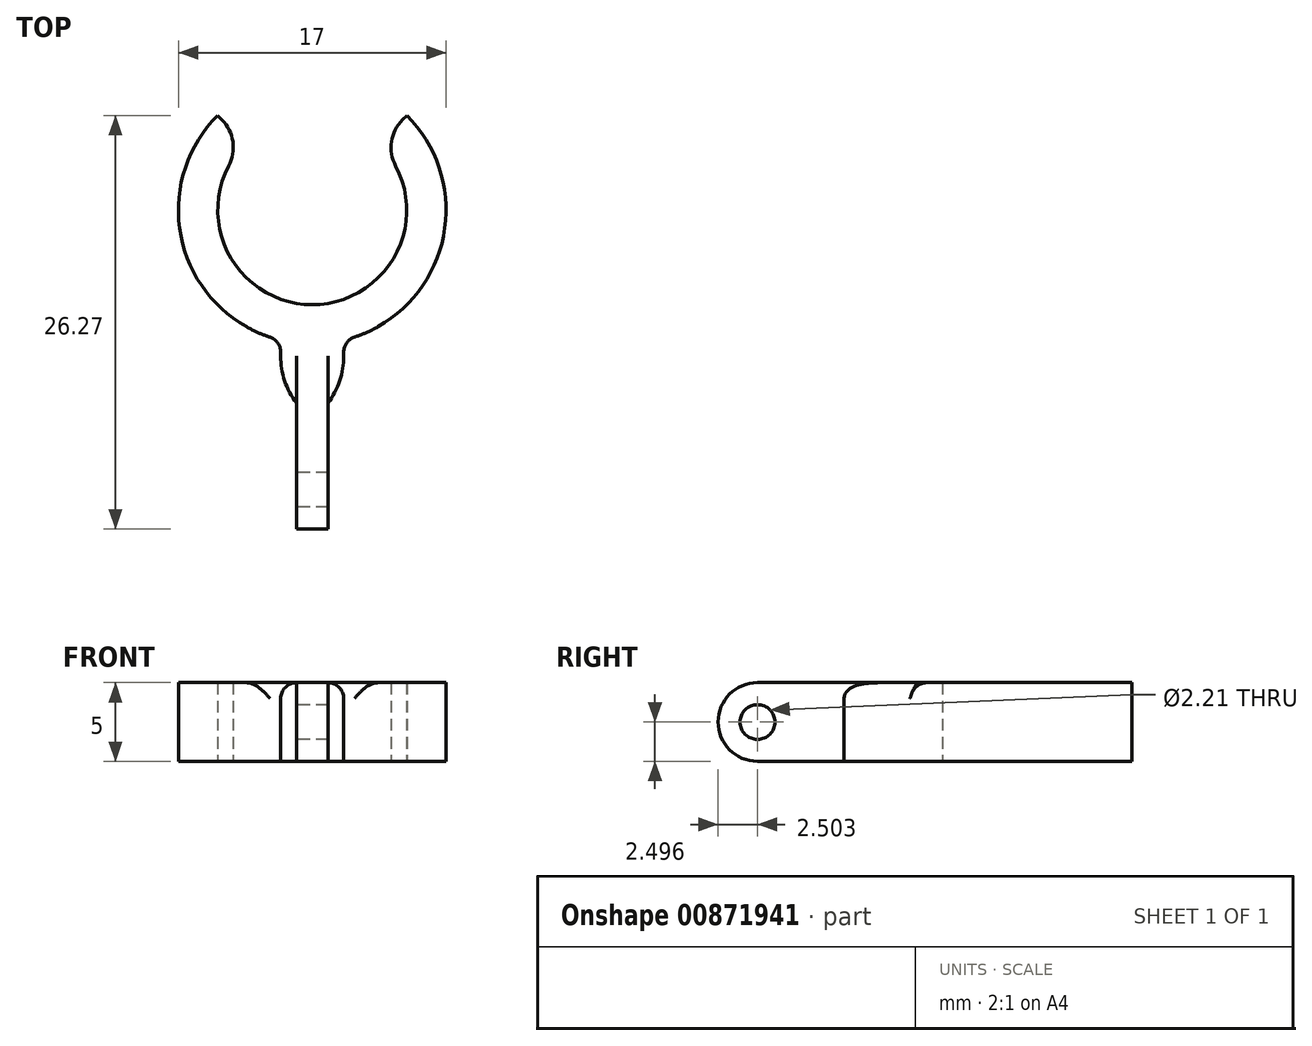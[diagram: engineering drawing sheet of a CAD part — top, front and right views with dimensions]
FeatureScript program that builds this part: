
annotation { "Feature Type Name" : "Feature", "Feature Type Description" : "" }
export const myFeature = defineFeature(function(context is Context, id is Id, definition is map)
    precondition{}
    {
        {
            var Q0;
            Q0=qCreatedBy(makeId("Top.planeOp"),FACE);
            var sketch = newSketch(context, id + "F0", { "sketchPlane" : qUnion([Q0])});
            skArc(sketch, "E0", {"start": v(-4.24, 4.24) * mm, "mid": v(0, -6) * mm, "end": v(4.24, 4.24) * mm});
            skArc(sketch, "E1", {"start": v(-6.01, 6.01) * mm, "mid": v(-8.18, -2.3) * mm, "end": v(-2, -8.26) * mm});
            skLineSegment(sketch, "E2", {"start": v(0, 15.66) * mm, "end": v(0, -18.54) * mm, "construction": true});
            skLineSegment(sketch, "E3", {"start": v(-4.24, 4.24) * mm, "end": v(-6.01, 6.01) * mm});
            skLineSegment(sketch, "E4", {"start": v(4.24, 4.24) * mm, "end": v(6.01, 6.01) * mm});
            skLineSegment(sketch, "E5", {"start": v(-2, -8.26) * mm, "end": v(-2, -12.26) * mm});
            skLineSegment(sketch, "E6", {"start": v(-2, -12.26) * mm, "end": v(-1, -12.26) * mm});
            skLineSegment(sketch, "E7", {"start": v(-1, -12.26) * mm, "end": v(-1, -20.26) * mm});
            skLineSegment(sketch, "E8", {"start": v(-1, -20.26) * mm, "end": v(0, -20.26) * mm});
            skLineSegment(sketch, "E9.MirrorCS", {"start": v(2, -8.26) * mm, "end": v(2, -12.26) * mm});
            skLineSegment(sketch, "E10.MirrorCS", {"start": v(2, -12.26) * mm, "end": v(1, -12.26) * mm});
            skLineSegment(sketch, "E11.MirrorCS", {"start": v(1, -12.26) * mm, "end": v(1, -20.26) * mm});
            skLineSegment(sketch, "E12.MirrorCS", {"start": v(1, -20.26) * mm, "end": v(0, -20.26) * mm});
            skArc(sketch, "E13.trimOffspring", {"start": v(2, -8.26) * mm, "mid": v(8.18, -2.3) * mm, "end": v(6.01, 6.01) * mm});
            skSolve(sketch);
        }
        {
            var Q0;
            Q0 = qSketchRegion(id + "F0", true);
            extrude(context, id + "F1", {"entities" : qUnion([Q0]), "depth" : 5 * mm, "offsetDistance" : 25 * mm});
        }
        {
            var Q0;
            Q0=makeQuery(id+"F1.opExtrude","SWEPT_FACE",FACE,{"disambiguationData":[OSD([sQuery(id+"F0.wireOp",EDGE,"E7")])]});
            var sketch = newSketch(context, id + "F2", { "sketchPlane" : qUnion([Q0])});
            skCircle(sketch, "E14", {"center": v(17.76, 2.5) * mm, "radius": 1.1 * mm});
            skSolve(sketch);
        }
        {
            var Q0;
            Q0=makeQuery(id+"F2.imprint","IMPRINT",FACE,{"disambiguationData":[TD([[makeQuery(id+"F2.imprint","IMPRINT",EDGE,{"derivedFrom":sQuery(id+"F2.wireOp",EDGE,"E14")}),1.0]])]});
            extrude(context, id + "F3", {"entities" : qUnion([Q0]), "operationType" : NewBodyOperationType.REMOVE, "oppositeDirection" : true, "depth" : 5 * mm, "offsetDistance" : 25 * mm});
        }
        {
            var Q0;
            Q0=makeQuery(id+"F1.opExtrude","SWEPT_EDGE",EDGE,{"disambiguationData":[OSD([sQuery(id+"F0.wireOp",EDGE,"E0"),sQuery(id+"F0.wireOp",EDGE,"E4")])]});
            var Q1;
            Q1=makeQuery(id+"F1.opExtrude","SWEPT_EDGE",EDGE,{"disambiguationData":[OSD([sQuery(id+"F0.wireOp",EDGE,"E0"),sQuery(id+"F0.wireOp",EDGE,"E3")])]});
            fillet(context, id + "F4", {"entities" : qUnion([Q0, Q1]), "radius" : 2.5 * mm, "tangentPropagation" : true, "allowEdgeOverflow" : false});
        }
        {
            var Q0;
            Q0=makeQuery(id+"F1.opExtrude","SWEPT_EDGE",EDGE,{"disambiguationData":[OSD([sQuery(id+"F0.wireOp",EDGE,"E9.MirrorCS"),sQuery(id+"F0.wireOp",EDGE,"E10.MirrorCS")])]});
            var Q1;
            Q1=makeQuery(id+"F1.opExtrude","SWEPT_EDGE",EDGE,{"disambiguationData":[OSD([sQuery(id+"F0.wireOp",EDGE,"E5"),sQuery(id+"F0.wireOp",EDGE,"E6")])]});
            fillet(context, id + "F5", {"entities" : qUnion([Q0, Q1]), "radius" : 5 * mm, "tangentPropagation" : true, "allowEdgeOverflow" : false});
        }
        {
            var Q0;
            Q0=makeQuery(id+"F1.opExtrude","SWEPT_EDGE",EDGE,{"disambiguationData":[OSD([sQuery(id+"F0.wireOp",EDGE,"E1"),sQuery(id+"F0.wireOp",EDGE,"E5")])]});
            var Q1;
            Q1=makeQuery(id+"F1.opExtrude","SWEPT_EDGE",EDGE,{"disambiguationData":[OSD([sQuery(id+"F0.wireOp",EDGE,"E9.MirrorCS"),sQuery(id+"F0.wireOp",EDGE,"E13.trimOffspring")])]});
            var Q2;
            {var subQ0=sQuery(id+"F0.wireOp",EDGE,"E10.MirrorCS");var subQ1=sQuery(id+"F0.wireOp",EDGE,"E9.MirrorCS");Q2=makeQuery(id+"F5.opFillet","BLEND_EDGE",EDGE,{"blendedFrom":[makeQuery(id+"F1.opExtrude","SWEPT_EDGE",EDGE,{"disambiguationData":[OSD([subQ1,subQ0])]}),makeQuery(id+"F1.opExtrude","CAP_FACE",FACE,{"disambiguationData":[OSD([sQuery(id+"F0.wireOp",EDGE,"E0"),sQuery(id+"F0.wireOp",EDGE,"E1"),sQuery(id+"F0.wireOp",EDGE,"E3"),sQuery(id+"F0.wireOp",EDGE,"E4"),sQuery(id+"F0.wireOp",EDGE,"E5"),sQuery(id+"F0.wireOp",EDGE,"E6"),sQuery(id+"F0.wireOp",EDGE,"E7"),sQuery(id+"F0.wireOp",EDGE,"E8"),subQ1,subQ0,sQuery(id+"F0.wireOp",EDGE,"E11.MirrorCS"),sQuery(id+"F0.wireOp",EDGE,"E12.MirrorCS"),sQuery(id+"F0.wireOp",EDGE,"E13.trimOffspring")])],"isStart":false})],"blendedInto":[makeQuery(id+"F1.opExtrude","CAP_FACE",FACE,{"disambiguationData":[OSD([sQuery(id+"F0.wireOp",EDGE,"E0"),sQuery(id+"F0.wireOp",EDGE,"E1"),sQuery(id+"F0.wireOp",EDGE,"E3"),sQuery(id+"F0.wireOp",EDGE,"E4"),sQuery(id+"F0.wireOp",EDGE,"E5"),sQuery(id+"F0.wireOp",EDGE,"E6"),sQuery(id+"F0.wireOp",EDGE,"E7"),sQuery(id+"F0.wireOp",EDGE,"E8"),subQ1,subQ0,sQuery(id+"F0.wireOp",EDGE,"E11.MirrorCS"),sQuery(id+"F0.wireOp",EDGE,"E12.MirrorCS"),sQuery(id+"F0.wireOp",EDGE,"E13.trimOffspring")])],"isStart":false})]});}
            var Q3;
            {var subQ0=sQuery(id+"F0.wireOp",EDGE,"E6");var subQ1=sQuery(id+"F0.wireOp",EDGE,"E5");Q3=makeQuery(id+"F5.opFillet","BLEND_EDGE",EDGE,{"blendedFrom":[makeQuery(id+"F1.opExtrude","SWEPT_EDGE",EDGE,{"disambiguationData":[OSD([subQ1,subQ0])]}),makeQuery(id+"F1.opExtrude","CAP_FACE",FACE,{"disambiguationData":[OSD([sQuery(id+"F0.wireOp",EDGE,"E0"),sQuery(id+"F0.wireOp",EDGE,"E1"),sQuery(id+"F0.wireOp",EDGE,"E3"),sQuery(id+"F0.wireOp",EDGE,"E4"),subQ1,subQ0,sQuery(id+"F0.wireOp",EDGE,"E7"),sQuery(id+"F0.wireOp",EDGE,"E8"),sQuery(id+"F0.wireOp",EDGE,"E9.MirrorCS"),sQuery(id+"F0.wireOp",EDGE,"E10.MirrorCS"),sQuery(id+"F0.wireOp",EDGE,"E11.MirrorCS"),sQuery(id+"F0.wireOp",EDGE,"E12.MirrorCS"),sQuery(id+"F0.wireOp",EDGE,"E13.trimOffspring")])],"isStart":false})],"blendedInto":[makeQuery(id+"F1.opExtrude","CAP_FACE",FACE,{"disambiguationData":[OSD([sQuery(id+"F0.wireOp",EDGE,"E0"),sQuery(id+"F0.wireOp",EDGE,"E1"),sQuery(id+"F0.wireOp",EDGE,"E3"),sQuery(id+"F0.wireOp",EDGE,"E4"),subQ1,subQ0,sQuery(id+"F0.wireOp",EDGE,"E7"),sQuery(id+"F0.wireOp",EDGE,"E8"),sQuery(id+"F0.wireOp",EDGE,"E9.MirrorCS"),sQuery(id+"F0.wireOp",EDGE,"E10.MirrorCS"),sQuery(id+"F0.wireOp",EDGE,"E11.MirrorCS"),sQuery(id+"F0.wireOp",EDGE,"E12.MirrorCS"),sQuery(id+"F0.wireOp",EDGE,"E13.trimOffspring")])],"isStart":false})]});}
            fillet(context, id + "F6", {"entities" : qUnion([Q0, Q1, Q2, Q3]), "radius" : 1 * mm, "tangentPropagation" : true, "allowEdgeOverflow" : false});
        }
        {
            var Q0;
            Q0=makeQuery(id+"F1.opExtrude","CAP_EDGE",EDGE,{"disambiguationData":[OSD([sQuery(id+"F0.wireOp",EDGE,"E8"),sQuery(id+"F0.wireOp",EDGE,"E12.MirrorCS")])],"isStart":false});
            var Q1;
            Q1=makeQuery(id+"F1.opExtrude","CAP_EDGE",EDGE,{"disambiguationData":[OSD([sQuery(id+"F0.wireOp",EDGE,"E8"),sQuery(id+"F0.wireOp",EDGE,"E12.MirrorCS")])],"isStart":true});
            fillet(context, id + "F7", {"entities" : qUnion([Q0, Q1]), "radius" : 2.5 * mm, "tangentPropagation" : true, "allowEdgeOverflow" : false});
        }
    });
